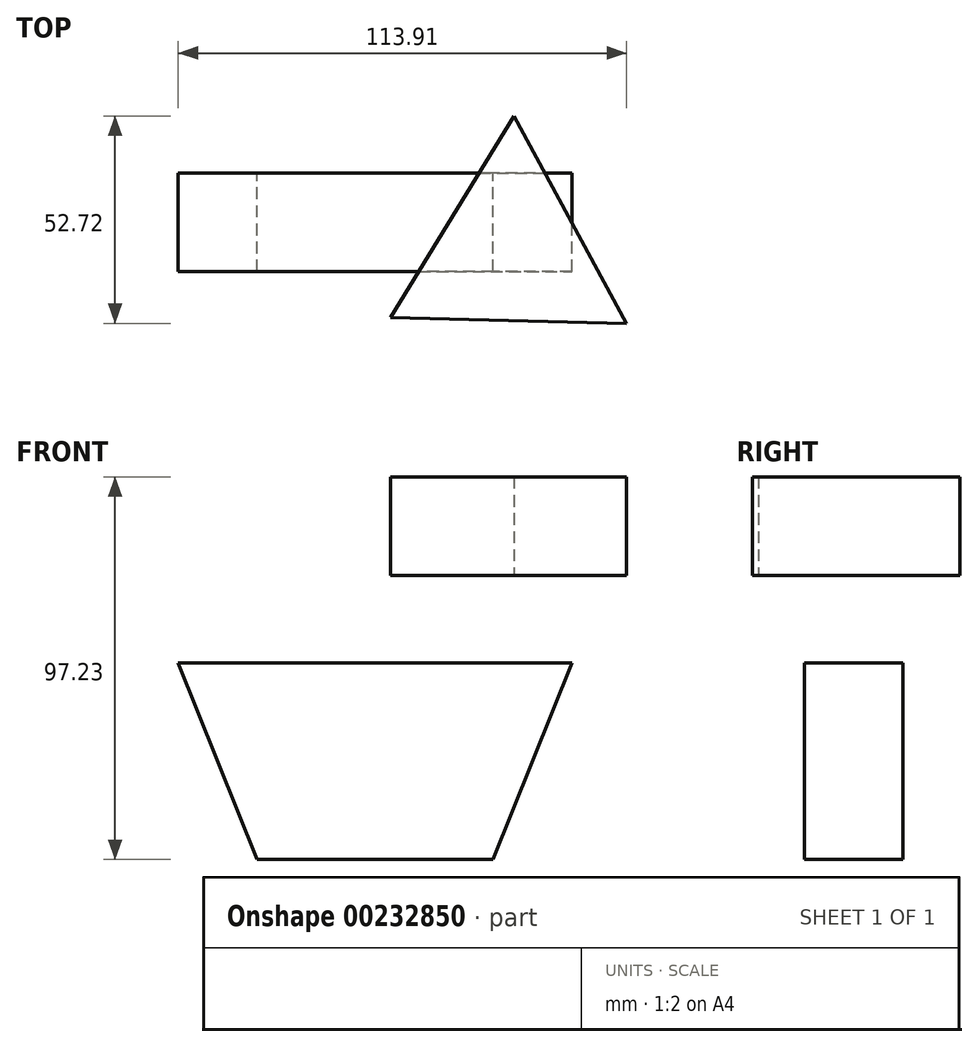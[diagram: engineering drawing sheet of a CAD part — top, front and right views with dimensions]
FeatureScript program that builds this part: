
annotation { "Feature Type Name" : "Feature", "Feature Type Description" : "" }
export const myFeature = defineFeature(function(context is Context, id is Id, definition is map)
    precondition{}
    {
        {
            var Q0;
            Q0=qCreatedBy(makeId("Top.planeOp"),FACE);
            var sketch = newSketch(context, id + "F0", { "sketchPlane" : qUnion([Q0])});
            skLineSegment(sketch, "E0", {"start": v(-26.07, -36.63) * mm, "end": v(5.26, 14.54) * mm});
            skLineSegment(sketch, "E1", {"start": v(5.26, 14.54) * mm, "end": v(33.9, -38.18) * mm});
            skLineSegment(sketch, "E2", {"start": v(33.9, -38.18) * mm, "end": v(-26.07, -36.63) * mm});
            skSolve(sketch);
        }
        {
            var Q0;
            Q0=qCreatedBy(makeId("Front.planeOp"),FACE);
            var sketch = newSketch(context, id + "F1", { "sketchPlane" : qUnion([Q0])});
            skLineSegment(sketch, "E3", {"start": v(-60, -72.23) * mm, "end": v(-80, -22.23) * mm});
            skLineSegment(sketch, "E4", {"start": v(-80, -22.23) * mm, "end": v(20, -22.23) * mm});
            skLineSegment(sketch, "E5", {"start": v(20, -22.23) * mm, "end": v(0, -72.23) * mm});
            skLineSegment(sketch, "E6", {"start": v(0, -72.23) * mm, "end": v(-60, -72.23) * mm});
            skLineSegment(sketch, "E7", {"start": v(-80, -22.23) * mm, "end": v(-80, -90.1) * mm});
            skLineSegment(sketch, "E8", {"start": v(20, -22.23) * mm, "end": v(20, -81.23) * mm});
            skSolve(sketch);
        }
        {
            var Q0;
            Q0=makeQuery(id+"F0.imprint","IMPRINT",FACE,{"disambiguationData":[TD([[makeQuery(id+"F0.imprint","IMPRINT",EDGE,{"derivedFrom":sQuery(id+"F0.wireOp",EDGE,"E0")}),-1.0]])]});
            extrude(context, id + "F2", {"entities" : qUnion([Q0]), "depth" : 25 * mm});
        }
        {
            var Q0;
            Q0=makeQuery(id+"F1.imprint","IMPRINT",FACE,{"disambiguationData":[TD([[makeQuery(id+"F1.imprint","IMPRINT",EDGE,{"derivedFrom":sQuery(id+"F1.wireOp",EDGE,"E3")}),-1.0]])]});
            extrude(context, id + "F3", {"entities" : qUnion([Q0]), "depth" : 25 * mm});
        }
    });
